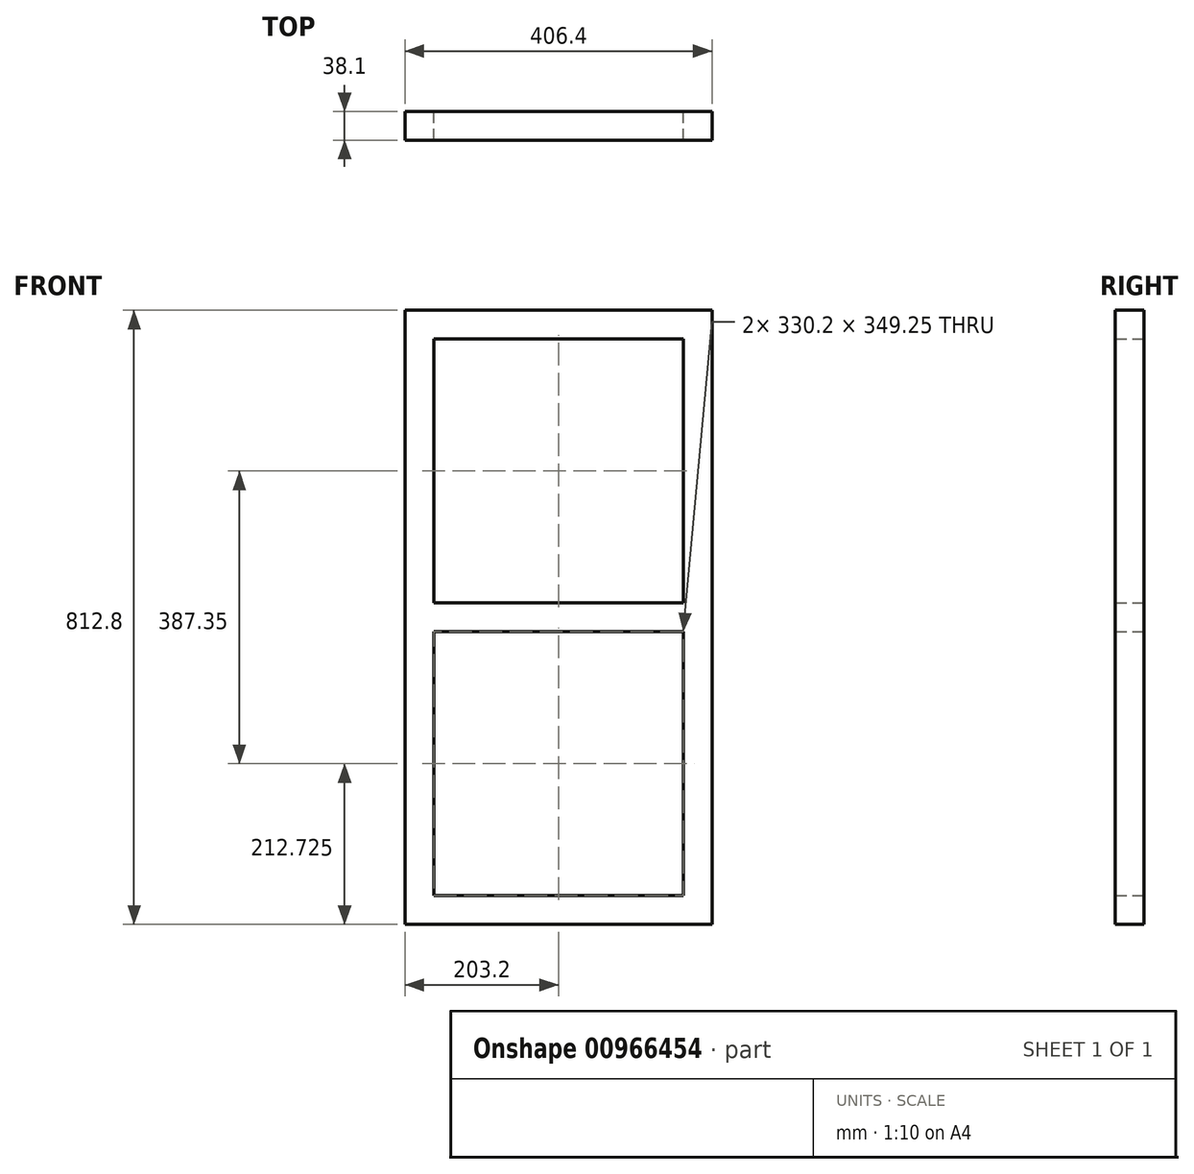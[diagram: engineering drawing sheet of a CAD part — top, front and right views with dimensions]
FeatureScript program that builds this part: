
annotation { "Feature Type Name" : "Feature", "Feature Type Description" : "" }
export const myFeature = defineFeature(function(context is Context, id is Id, definition is map)
    precondition{}
    {
        {
            var Q0;
            Q0=qCreatedBy(makeId("Front.planeOp"),FACE);
            var sketch = newSketch(context, id + "F0", { "sketchPlane" : qUnion([Q0])});
            skLineSegment(sketch, "E0.bottom", {"start": v(203.2, -406.4) * mm, "end": v(-203.2, -406.4) * mm});
            skLineSegment(sketch, "E0.top", {"start": v(203.2, 406.4) * mm, "end": v(-203.2, 406.4) * mm});
            skLineSegment(sketch, "E0.left", {"start": v(203.2, -406.4) * mm, "end": v(203.2, 406.4) * mm});
            skLineSegment(sketch, "E0.right", {"start": v(-203.2, -406.4) * mm, "end": v(-203.2, 406.4) * mm});
            skPoint(sketch, "E0.middle", {"position": v(0, 0) * mm});
            skLineSegment(sketch, "E1.bottom", {"start": v(165.1, -368.3) * mm, "end": v(-165.1, -368.3) * mm});
            skLineSegment(sketch, "E1.top", {"start": v(165.1, 368.3) * mm, "end": v(-165.1, 368.3) * mm});
            skLineSegment(sketch, "E1.left", {"start": v(165.1, -368.3) * mm, "end": v(165.1, 368.3) * mm});
            skLineSegment(sketch, "E1.right", {"start": v(-165.1, -368.3) * mm, "end": v(-165.1, 368.3) * mm});
            skLineSegment(sketch, "E2.bottom", {"start": v(165.1, -19.05) * mm, "end": v(-165.1, -19.05) * mm});
            skLineSegment(sketch, "E2.top", {"start": v(165.1, 19.05) * mm, "end": v(-165.1, 19.05) * mm});
            skLineSegment(sketch, "E2.left", {"start": v(165.1, -19.05) * mm, "end": v(165.1, 19.05) * mm});
            skLineSegment(sketch, "E2.right", {"start": v(-165.1, -19.05) * mm, "end": v(-165.1, 19.05) * mm});
            skSolve(sketch);
        }
        {
            var Q0;
            Q0=makeQuery(id+"F0.imprint","IMPRINT",FACE,{"disambiguationData":[TD([[makeQuery(id+"F0.imprint","IMPRINT",EDGE,{"derivedFrom":sQuery(id+"F0.wireOp",EDGE,"E0.bottom")}),-1.0]])]});
            var Q1;
            {var subQ2=sQuery(id+"F0.wireOp",EDGE,"E2.bottom");Q1=makeQuery(id+"F0.imprint","IMPRINT",FACE,{"disambiguationData":[TD([[makeQuery(id+"F0.imprint","IMPRINT",EDGE,{"derivedFrom":subQ2}),-1.0]])]});}
            extrude(context, id + "F1", {"entities" : qUnion([Q0, Q1]), "depth" : 38.1 * mm, "offsetDistance" : 25.4 * mm});
        }
    });
